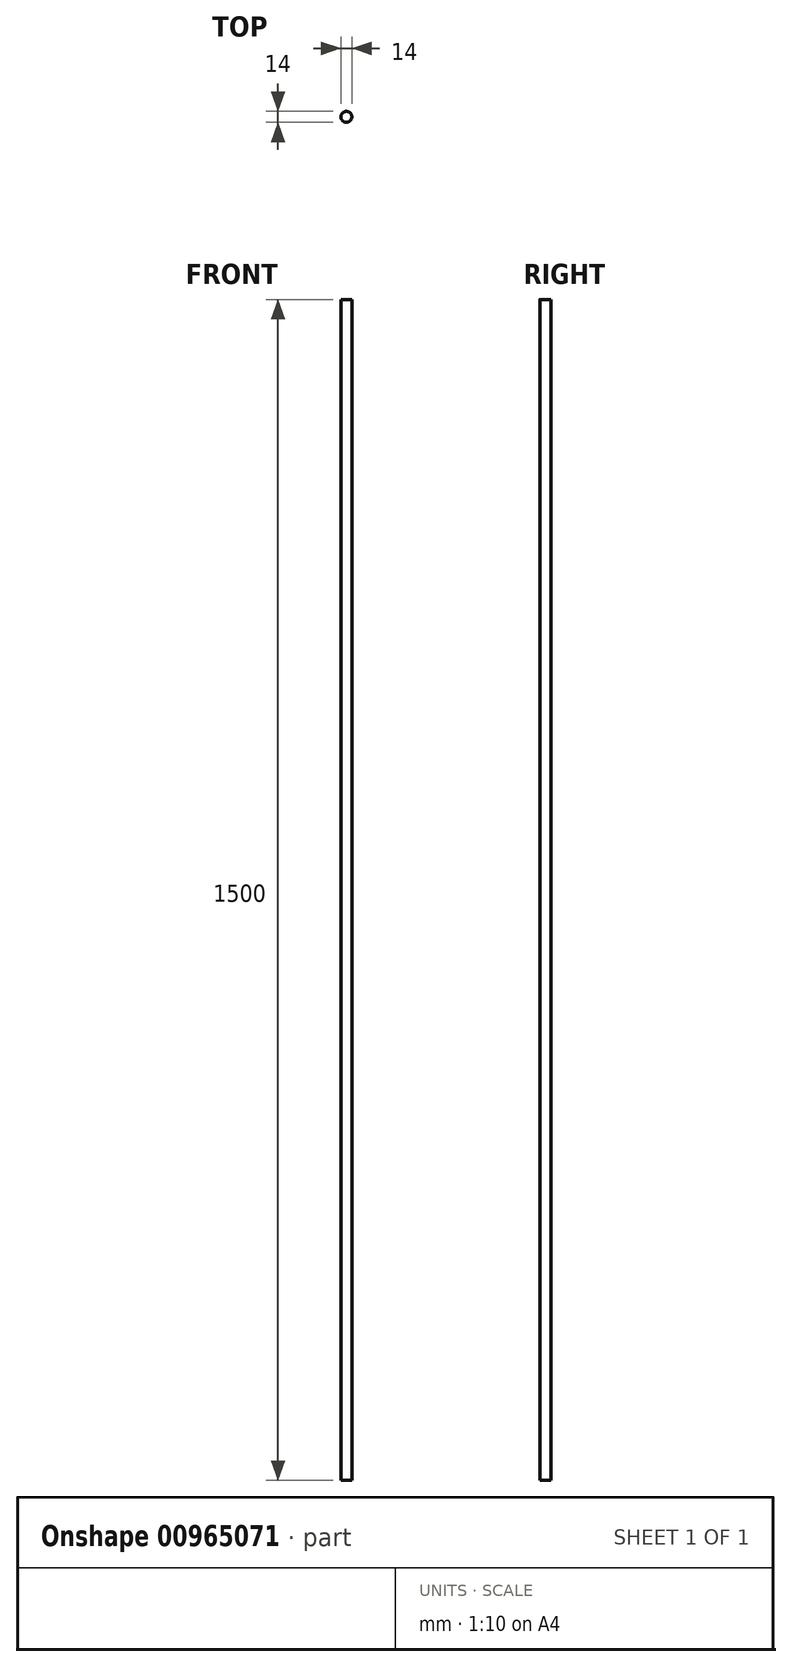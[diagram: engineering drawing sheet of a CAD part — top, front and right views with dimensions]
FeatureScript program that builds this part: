
annotation { "Feature Type Name" : "Feature", "Feature Type Description" : "" }
export const myFeature = defineFeature(function(context is Context, id is Id, definition is map)
    precondition{}
    {
        {
            var Q0;
            Q0=qCreatedBy(makeId("Top.planeOp"),FACE);
            var sketch = newSketch(context, id + "F0", { "sketchPlane" : qUnion([Q0])});
            skCircle(sketch, "E0", {"center": v(0, 0) * mm, "radius": 7 * mm});
            skSolve(sketch);
        }
        {
            var Q0;
            Q0=makeQuery(id+"F0.imprint","IMPRINT",FACE,{"disambiguationData":[TD([[makeQuery(id+"F0.imprint","IMPRINT",EDGE,{"derivedFrom":sQuery(id+"F0.wireOp",EDGE,"E0")}),1.0]])]});
            extrude(context, id + "F1", {"entities" : qUnion([Q0]), "depth" : 1500 * mm, "offsetDistance" : 25 * mm});
        }
    });
